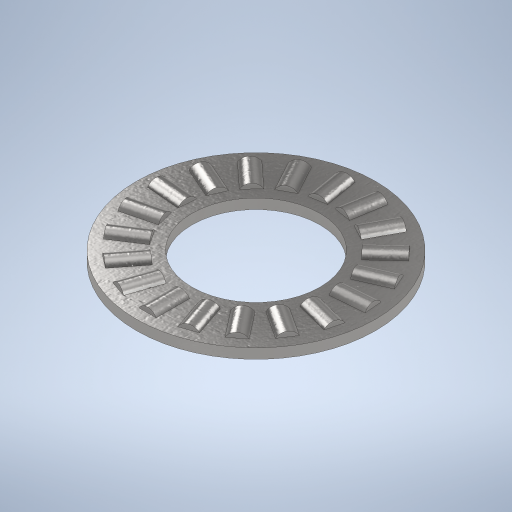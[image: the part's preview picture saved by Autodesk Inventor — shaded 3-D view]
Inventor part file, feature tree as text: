
AUTODESK INVENTOR PART (.ipt)
format: ipt  version: 2024 (Build 280153000, 153)  size: 455,680 bytes
history: native  units: in
note: dims shown in document units (in); Inventor stores cm internally (conversion verified against a paired STEP export)
features: other x18, revolve x1, pattern_circular x1
ambient origin geometry x8: Origin, YZ Plane, XZ Plane, XY Plane, X Axis, Y Axis, Z Axis, Center Point
bodies: Solid1 (feature_tree), Solid2 (feature_tree), Solid3 (feature_tree), Solid4 (feature_tree), Solid5 (feature_tree), Solid6 (feature_tree), Solid7 (feature_tree), Solid8 (feature_tree), Solid9 (feature_tree), Solid10 (feature_tree), Solid11 (feature_tree), Solid12 (feature_tree), Solid13 (feature_tree), Solid14 (feature_tree), Solid15 (feature_tree), Solid16 (feature_tree), Solid17 (feature_tree), Solid18 (feature_tree), Solid19 (feature_tree), Solid20 (feature_tree)
feature tree (20):
  revolve  "Revolve2"  [1 undecoded]
  other  "CirPattern1[1]"
  other  "CirPattern1[2]"
  other  "CirPattern1[3]"
  other  "CirPattern1[4]"
  other  "CirPattern1[5]"
  other  "CirPattern1[6]"
  other  "CirPattern1[7]"
  other  "CirPattern1[8]"
  other  "CirPattern1[9]"
  other  "CirPattern1[10]"
  other  "CirPattern1[11]"
  other  "CirPattern1[12]"
  other  "CirPattern1[13]"
  other  "CirPattern1[14]"
  other  "CirPattern1[15]"
  other  "CirPattern1[16]"
  other  "CirPattern1[17]"
  other  "CirPattern1[18]"
  pattern_circular  "CirPattern2"
note: 1 required parameter value undecoded (feature->parameter linkage not recoverable at this tier; creation-order binding heuristic only, values carry confidence <= 0.55)
